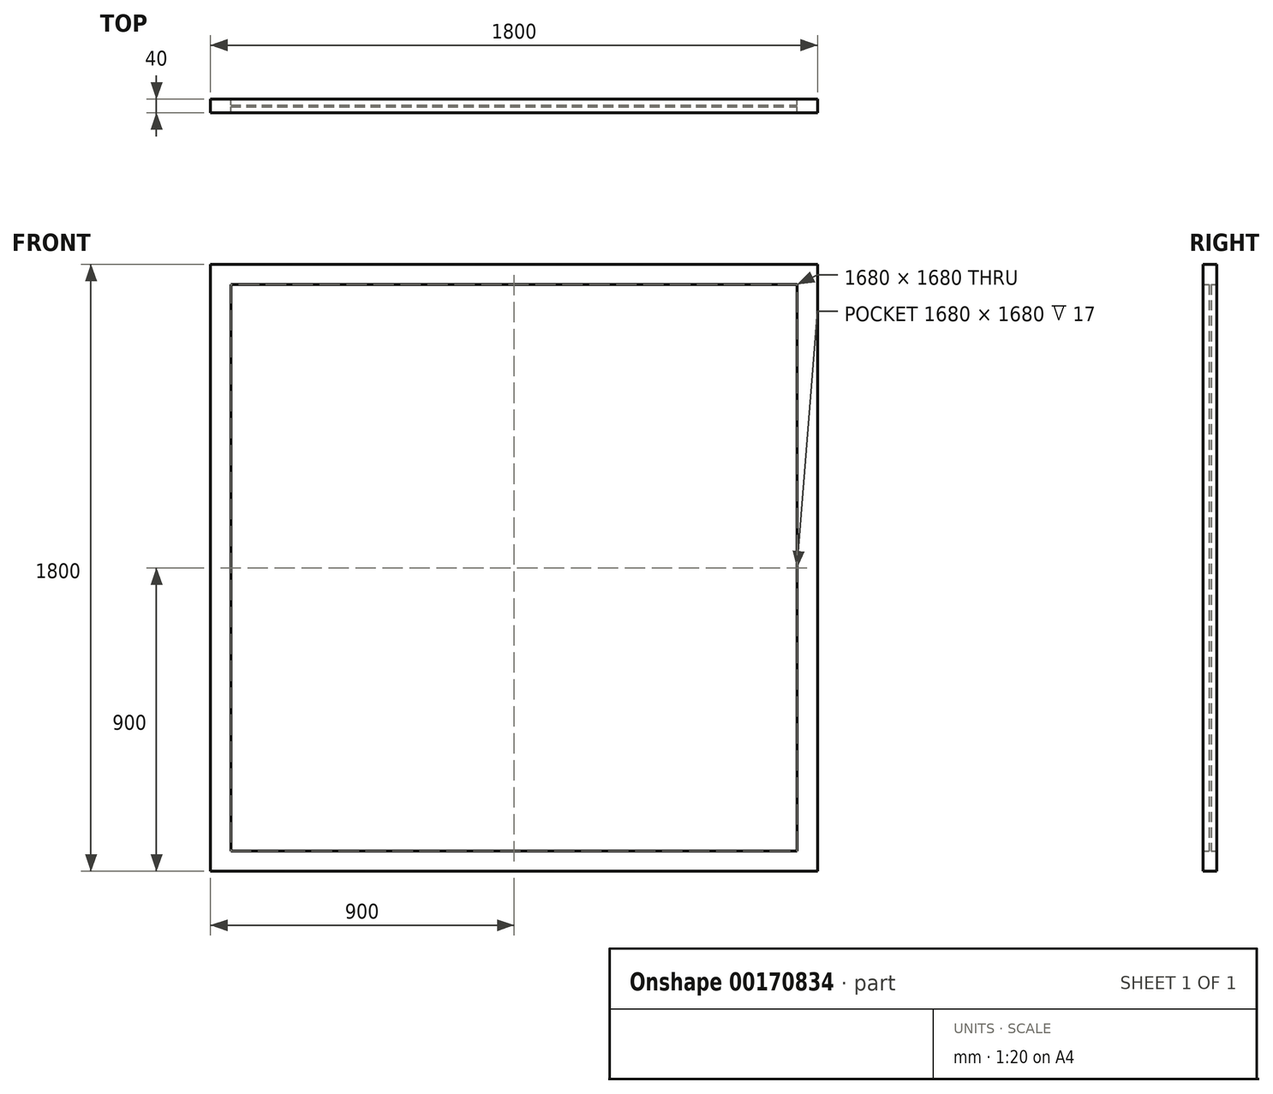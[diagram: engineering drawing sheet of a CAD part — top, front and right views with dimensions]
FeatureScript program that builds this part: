
annotation { "Feature Type Name" : "Feature", "Feature Type Description" : "" }
export const myFeature = defineFeature(function(context is Context, id is Id, definition is map)
    precondition{}
    {
        {
            var Q0;
            Q0=qCreatedBy(makeId("Front.planeOp"),FACE);
            var sketch = newSketch(context, id + "F0", { "sketchPlane" : qUnion([Q0])});
            skLineSegment(sketch, "E0.bottom", {"start": v(-900, 900) * mm, "end": v(900, 900) * mm});
            skLineSegment(sketch, "E0.top", {"start": v(-900, -900) * mm, "end": v(900, -900) * mm});
            skLineSegment(sketch, "E0.left", {"start": v(-900, 900) * mm, "end": v(-900, -900) * mm});
            skLineSegment(sketch, "E0.right", {"start": v(900, 900) * mm, "end": v(900, -900) * mm});
            skPoint(sketch, "E0.middle", {"position": v(0, 0) * mm});
            skLineSegment(sketch, "E1.0", {"start": v(-840, 840) * mm, "end": v(840, 840) * mm});
            skLineSegment(sketch, "E1.1", {"start": v(-840, 840) * mm, "end": v(-840, -840) * mm});
            skLineSegment(sketch, "E1.2", {"start": v(-840, -840) * mm, "end": v(840, -840) * mm});
            skLineSegment(sketch, "E1.3", {"start": v(840, 840) * mm, "end": v(840, -840) * mm});
            skSolve(sketch);
        }
        {
            var Q0;
            Q0=makeQuery(id+"F0.imprint","IMPRINT",FACE,{"disambiguationData":[TD([[makeQuery(id+"F0.imprint","IMPRINT",EDGE,{"derivedFrom":sQuery(id+"F0.wireOp",EDGE,"E0.bottom")}),-1.0]])]});
            extrude(context, id + "F1", {"entities" : qUnion([Q0]), "endBound" : BoundingType.SYMMETRIC, "depth" : 40 * mm});
        }
        {
            var Q0;
            Q0=makeQuery(id+"F0.imprint","IMPRINT",FACE,{"disambiguationData":[TD([[makeQuery(id+"F0.imprint","IMPRINT",EDGE,{"derivedFrom":sQuery(id+"F0.wireOp",EDGE,"E1.0")}),-1.0]])]});
            extrude(context, id + "F2", {"entities" : qUnion([Q0]), "operationType" : NewBodyOperationType.ADD, "endBound" : BoundingType.SYMMETRIC, "depth" : 6 * mm});
        }
    });
